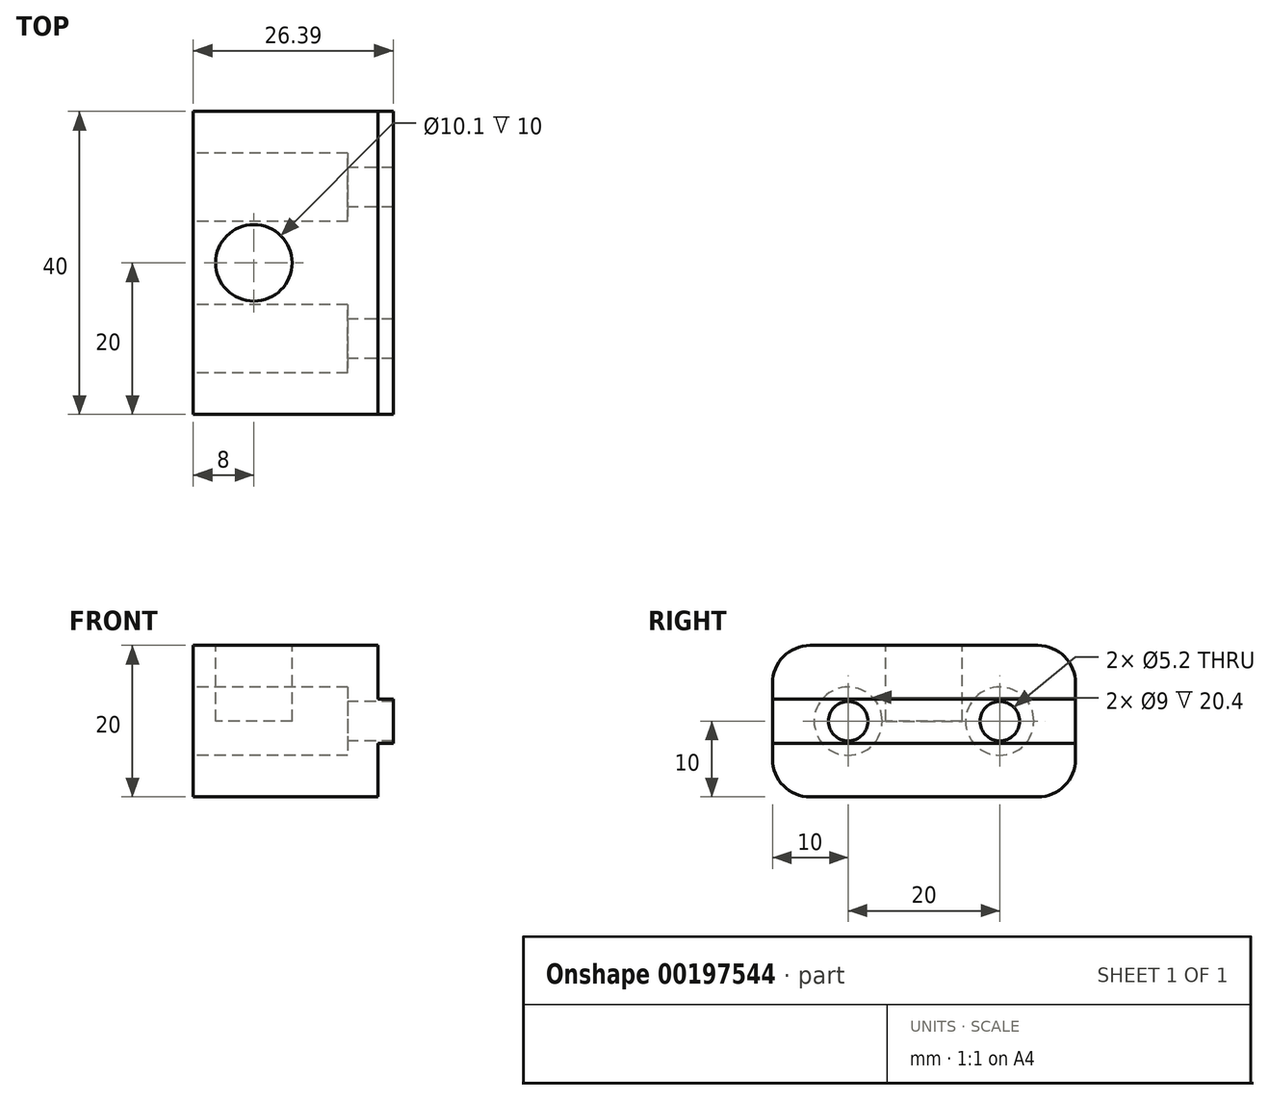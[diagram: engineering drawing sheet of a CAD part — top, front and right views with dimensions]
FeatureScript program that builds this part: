
annotation { "Feature Type Name" : "Feature", "Feature Type Description" : "" }
export const myFeature = defineFeature(function(context is Context, id is Id, definition is map)
    precondition{}
    {
        {
            var Q0;
            Q0=qCreatedBy(makeId("Top.planeOp"),FACE);
            var sketch = newSketch(context, id + "F0", { "sketchPlane" : qUnion([Q0])});
            skLineSegment(sketch, "E0", {"start": v(-8, 20) * mm, "end": v(16.4, 20) * mm});
            skLineSegment(sketch, "E1", {"start": v(16.4, 20) * mm, "end": v(16.4, -20) * mm});
            skLineSegment(sketch, "E2", {"start": v(-8, 20) * mm, "end": v(-8, -20) * mm});
            skLineSegment(sketch, "E3", {"start": v(-8, -20) * mm, "end": v(16.4, -20) * mm});
            skSolve(sketch);
        }
        {
            var Q0;
            Q0=qSketchRegion(id+"F0",true);
            extrude(context, id + "F1", {"entities" : qUnion([Q0]), "depth" : 20 * mm});
        }
        {
            var Q0;
            Q0=makeQuery(id+"F1.opExtrude","CAP_FACE",FACE,{"disambiguationData":[OSD([sQuery(id+"F0.wireOp",EDGE,"E0"),sQuery(id+"F0.wireOp",EDGE,"E1"),sQuery(id+"F0.wireOp",EDGE,"E2"),sQuery(id+"F0.wireOp",EDGE,"E3")])],"isStart":false});
            var sketch = newSketch(context, id + "F2", { "sketchPlane" : qUnion([Q0])});
            skCircle(sketch, "E4", {"center": v(0, 0) * mm, "radius": 5.05 * mm});
            skSolve(sketch);
        }
        {
            var Q0;
            Q0=qSketchRegion(id+"F2",true);
            extrude(context, id + "F3", {"entities" : qUnion([Q0]), "operationType" : NewBodyOperationType.REMOVE, "oppositeDirection" : true, "depth" : 10 * mm});
        }
        {
            var Q0;
            Q0=makeQuery(id+"F1.opExtrude","SWEPT_FACE",FACE,{"disambiguationData":[OSD([sQuery(id+"F0.wireOp",EDGE,"E1")])]});
            var sketch = newSketch(context, id + "F4", { "sketchPlane" : qUnion([Q0])});
            skLineSegment(sketch, "E5.bottom", {"start": v(-20, 12.9) * mm, "end": v(20, 12.9) * mm});
            skLineSegment(sketch, "E5.top", {"start": v(-20, 7.1) * mm, "end": v(20, 7.1) * mm});
            skLineSegment(sketch, "E5.left", {"start": v(-20, 12.9) * mm, "end": v(-20, 7.1) * mm});
            skLineSegment(sketch, "E5.right", {"start": v(20, 12.9) * mm, "end": v(20, 7.1) * mm});
            skSolve(sketch);
        }
        {
            var Q0;
            Q0=qSketchRegion(id+"F4",true);
            extrude(context, id + "F5", {"entities" : qUnion([Q0]), "operationType" : NewBodyOperationType.ADD, "depth" : 2 * mm});
        }
        {
            var Q0;
            Q0=makeQuery(id+"F1.opExtrude","SWEPT_FACE",FACE,{"disambiguationData":[OSD([sQuery(id+"F0.wireOp",EDGE,"E2")])]});
            var sketch = newSketch(context, id + "F6", { "sketchPlane" : qUnion([Q0])});
            skCircle(sketch, "E6", {"center": v(-10, 10) * mm, "radius": 2.6 * mm});
            skPoint(sketch, "E6.centerSnap0", {"position": v(-20, 10) * mm});
            skCircle(sketch, "E7", {"center": v(10, 10) * mm, "radius": 2.6 * mm});
            skPoint(sketch, "E7.centerSnap0", {"position": v(20, 10) * mm});
            skSolve(sketch);
        }
        {
            var Q0;
            Q0=qSketchRegion(id+"F6",true);
            extrude(context, id + "F7", {"entities" : qUnion([Q0]), "operationType" : NewBodyOperationType.REMOVE, "endBound" : BoundingType.THROUGH_ALL, "oppositeDirection" : true, "depth" : 25 * mm});
        }
        {
            var Q0;
            Q0=makeQuery(id+"F1.opExtrude","SWEPT_FACE",FACE,{"disambiguationData":[OSD([sQuery(id+"F0.wireOp",EDGE,"E2")])]});
            var sketch = newSketch(context, id + "F8", { "sketchPlane" : qUnion([Q0])});
            skCircle(sketch, "E8.0", {"center": v(-10, 10) * mm, "radius": 2.6 * mm, "construction": true});
            skCircle(sketch, "E9.0", {"center": v(10, 10) * mm, "radius": 2.6 * mm, "construction": true});
            skCircle(sketch, "E10", {"center": v(-10, 10) * mm, "radius": 4.5 * mm});
            skCircle(sketch, "E11", {"center": v(10, 10) * mm, "radius": 4.5 * mm});
            skSolve(sketch);
        }
        {
            var Q0;
            Q0=qSketchRegion(id+"F8",true);
            extrude(context, id + "F9", {"entities" : qUnion([Q0]), "operationType" : NewBodyOperationType.REMOVE, "oppositeDirection" : true, "depth" : 20.4 * mm});
        }
        {
            var Q0;
            Q0=makeQuery(id+"F1.opExtrude","CAP_EDGE",EDGE,{"disambiguationData":[OSD([sQuery(id+"F0.wireOp",EDGE,"E3")])],"isStart":false});
            var Q1;
            Q1=makeQuery(id+"F1.opExtrude","CAP_EDGE",EDGE,{"disambiguationData":[OSD([sQuery(id+"F0.wireOp",EDGE,"E0")])],"isStart":false});
            var Q2;
            Q2=makeQuery(id+"F1.opExtrude","CAP_EDGE",EDGE,{"disambiguationData":[OSD([sQuery(id+"F0.wireOp",EDGE,"E3")])],"isStart":true});
            var Q3;
            Q3=makeQuery(id+"F1.opExtrude","CAP_EDGE",EDGE,{"disambiguationData":[OSD([sQuery(id+"F0.wireOp",EDGE,"E0")])],"isStart":true});
            fillet(context, id + "F10", {"entities" : qUnion([Q0, Q1, Q2, Q3]), "radius" : 5 * mm, "tangentPropagation" : true, "allowEdgeOverflow" : false});
        }
    });
